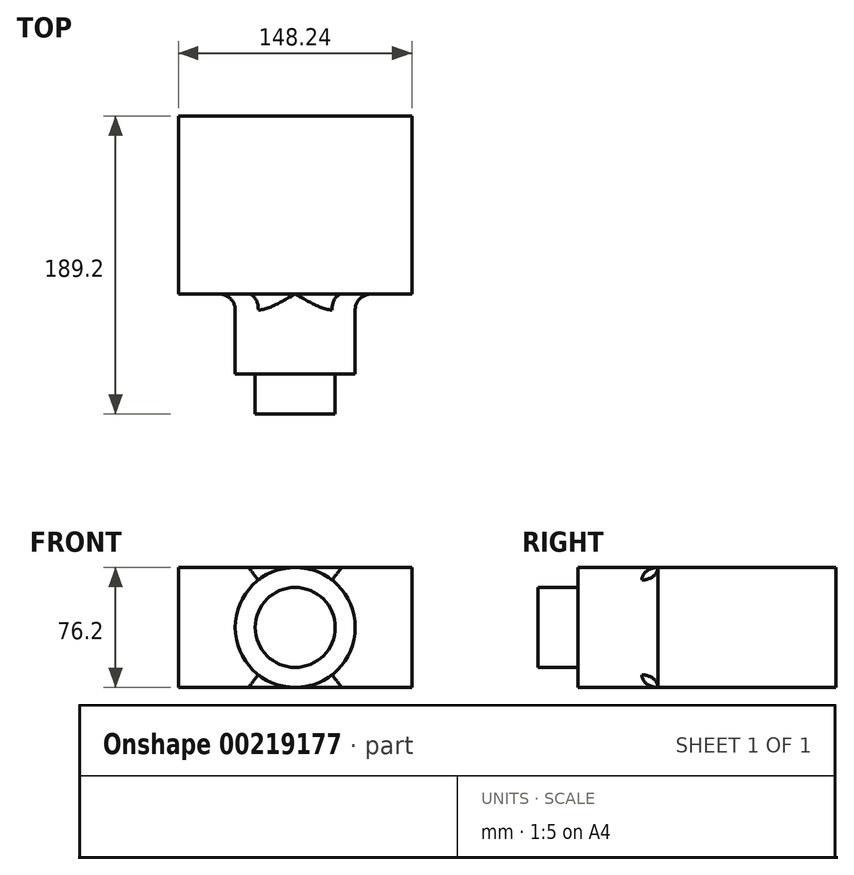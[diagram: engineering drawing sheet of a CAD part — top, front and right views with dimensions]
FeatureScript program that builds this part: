
annotation { "Feature Type Name" : "Feature", "Feature Type Description" : "" }
export const myFeature = defineFeature(function(context is Context, id is Id, definition is map)
    precondition{}
    {
        {
            var Q0;
            Q0=qCreatedBy(makeId("Top.planeOp"),FACE);
            var sketch = newSketch(context, id + "F0", { "sketchPlane" : qUnion([Q0])});
            skLineSegment(sketch, "E0.bottom", {"start": v(-44.61, 59.36) * mm, "end": v(103.63, 59.36) * mm});
            skLineSegment(sketch, "E0.top", {"start": v(-44.61, -53.64) * mm, "end": v(103.63, -53.64) * mm});
            skLineSegment(sketch, "E0.left", {"start": v(-44.61, 59.36) * mm, "end": v(-44.61, -53.64) * mm});
            skLineSegment(sketch, "E0.right", {"start": v(103.63, 59.36) * mm, "end": v(103.63, -53.64) * mm});
            skSolve(sketch);
        }
        {
            var Q0;
            Q0=makeQuery(id+"F0.imprint","IMPRINT",FACE,{"disambiguationData":[TD([[makeQuery(id+"F0.imprint","IMPRINT",EDGE,{"derivedFrom":sQuery(id+"F0.wireOp",EDGE,"E0.bottom")}),-1.0]])]});
            extrude(context, id + "F1", {"entities" : qUnion([Q0]), "depth" : 76.2 * mm, "offsetDistance" : 25.4 * mm});
        }
        {
            var Q0;
            Q0=makeQuery(id+"F1.opExtrude","SWEPT_FACE",FACE,{"disambiguationData":[OSD([sQuery(id+"F0.wireOp",EDGE,"E0.top")])]});
            var sketch = newSketch(context, id + "F2", { "sketchPlane" : qUnion([Q0])});
            skCircle(sketch, "E1", {"center": v(29.5, 38.1) * mm, "radius": 38.1 * mm});
            skPoint(sketch, "E1.centerSnap0", {"position": v(-44.61, 38.1) * mm});
            skPoint(sketch, "E1.centerSnap1", {"position": v(29.5, 76.2) * mm});
            skSolve(sketch);
        }
        {
            var Q0;
            {var subQ0=sQuery(id+"F2.wireOp",EDGE,"E1");var subQ1=sQuery(id+"F0.wireOp",EDGE,"E0.top");var subQ2=makeQuery(id+"F2.imprint","INTERSECT",VERTEX,{"derivedFrom":[makeQuery(id+"F1.opExtrude","CAP_EDGE",EDGE,{"disambiguationData":[OSD([subQ1])],"isStart":true}),subQ0]});Q0=makeQuery(id+"F2.imprint","IMPRINT",FACE,{"disambiguationData":[TD([[makeQuery(id+"F2.imprint","IMPRINT",EDGE,{"disambiguationData":[TD([[subQ2,-1.0]])],"derivedFrom":subQ0}),1.0]])]});}
            extrude(context, id + "F3", {"entities" : qUnion([Q0]), "operationType" : NewBodyOperationType.ADD, "depth" : 50.8 * mm, "offsetDistance" : 25.4 * mm});
        }
        {
            var Q0;
            Q0=makeQuery(id+"F3.boolean.opBoolean","SPLIT",EDGE,{"disambiguationData":[OD(1.0)],"derivedFrom":makeQuery(id+"F3.opExtrude","CAP_EDGE",EDGE,{"disambiguationData":[OSD([sQuery(id+"F2.wireOp",EDGE,"E1")])],"isStart":true})});
            var Q1;
            Q1=makeQuery(id+"F3.boolean.opBoolean","SPLIT",EDGE,{"disambiguationData":[OD(0.0)],"derivedFrom":makeQuery(id+"F3.opExtrude","CAP_EDGE",EDGE,{"disambiguationData":[OSD([sQuery(id+"F2.wireOp",EDGE,"E1")])],"isStart":true})});
            fillet(context, id + "F4", {"entities" : qUnion([Q0, Q1]), "tangentPropagation" : true, "radius" : 10.16 * mm, "defaultsChanged" : false, "vertexSettings" : [], "allowEdgeOverflow" : false});
        }
        {
            var Q0;
            Q0=makeQuery(id+"F3.opExtrude","CAP_FACE",FACE,{"disambiguationData":[OSD([sQuery(id+"F2.wireOp",EDGE,"E1")])],"isStart":false});
            var sketch = newSketch(context, id + "F5", { "sketchPlane" : qUnion([Q0])});
            skCircle(sketch, "E2", {"center": v(29.5, 38.1) * mm, "radius": 25.4 * mm});
            skSolve(sketch);
        }
        {
            var Q0;
            Q0=makeQuery(id+"F5.imprint","IMPRINT",FACE,{"disambiguationData":[TD([[makeQuery(id+"F5.imprint","IMPRINT",EDGE,{"derivedFrom":sQuery(id+"F5.wireOp",EDGE,"E2")}),1.0]])]});
            extrude(context, id + "F6", {"entities" : qUnion([Q0]), "operationType" : NewBodyOperationType.ADD, "depth" : 25.4 * mm, "offsetDistance" : 25.4 * mm});
        }
    });
